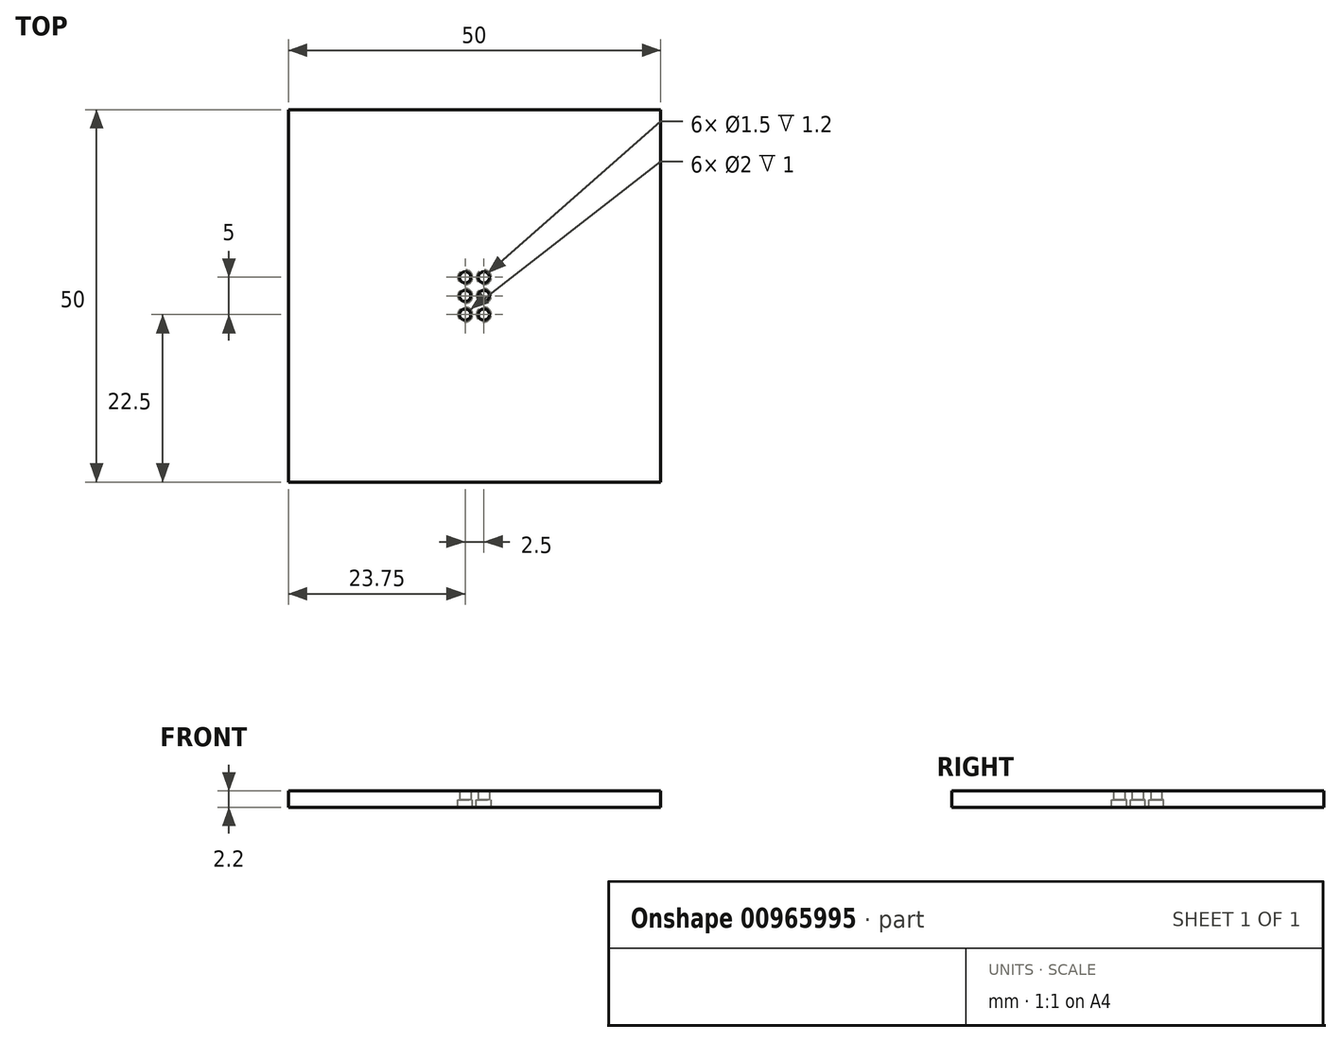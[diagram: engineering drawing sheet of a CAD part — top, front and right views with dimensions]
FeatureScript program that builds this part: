
annotation { "Feature Type Name" : "Feature", "Feature Type Description" : "" }
export const myFeature = defineFeature(function(context is Context, id is Id, definition is map)
    precondition{}
    {
        {
            var Q0;
            Q0=qCreatedBy(makeId("Top.planeOp"),FACE);
            var sketch = newSketch(context, id + "F0", { "sketchPlane" : qUnion([Q0])});
            skLineSegment(sketch, "E0.bottom", {"start": v(25, -25) * mm, "end": v(-25, -25) * mm});
            skLineSegment(sketch, "E0.top", {"start": v(25, 25) * mm, "end": v(-25, 25) * mm});
            skLineSegment(sketch, "E0.left", {"start": v(25, -25) * mm, "end": v(25, 25) * mm});
            skLineSegment(sketch, "E0.right", {"start": v(-25, -25) * mm, "end": v(-25, 25) * mm});
            skPoint(sketch, "E0.middle", {"position": v(0, 0) * mm});
            skCircle(sketch, "E1", {"center": v(-1.25, 0) * mm, "radius": 0.75 * mm});
            skCircle(sketch, "E2", {"center": v(-1.25, 2.5) * mm, "radius": 0.75 * mm});
            skCircle(sketch, "E3", {"center": v(-1.25, -2.5) * mm, "radius": 0.75 * mm});
            skCircle(sketch, "E4.MirrorC", {"center": v(1.25, 2.5) * mm, "radius": 0.75 * mm});
            skCircle(sketch, "E5.MirrorC", {"center": v(1.25, 0) * mm, "radius": 0.75 * mm});
            skCircle(sketch, "E6.MirrorC", {"center": v(1.25, -2.5) * mm, "radius": 0.75 * mm});
            skSolve(sketch);
        }
        {
            var Q0;
            Q0=makeQuery(id+"F0.imprint","IMPRINT",FACE,{"disambiguationData":[TD([[makeQuery(id+"F0.imprint","IMPRINT",EDGE,{"derivedFrom":sQuery(id+"F0.wireOp",EDGE,"E0.bottom")}),-1.0]])]});
            extrude(context, id + "F1", {"entities" : qUnion([Q0]), "depth" : 1.2 * mm, "offsetDistance" : 25 * mm});
        }
        {
            var Q0;
            Q0=makeQuery(id+"F1.opExtrude","CAP_FACE",FACE,{"disambiguationData":[OSD([sQuery(id+"F0.wireOp",EDGE,"E0.bottom"),sQuery(id+"F0.wireOp",EDGE,"E0.top"),sQuery(id+"F0.wireOp",EDGE,"E0.left"),sQuery(id+"F0.wireOp",EDGE,"E0.right"),sQuery(id+"F0.wireOp",EDGE,"E1"),sQuery(id+"F0.wireOp",EDGE,"E2"),sQuery(id+"F0.wireOp",EDGE,"E3"),sQuery(id+"F0.wireOp",EDGE,"E4.MirrorC"),sQuery(id+"F0.wireOp",EDGE,"E5.MirrorC"),sQuery(id+"F0.wireOp",EDGE,"E6.MirrorC")])],"isStart":true});
            var sketch = newSketch(context, id + "F2", { "sketchPlane" : qUnion([Q0])});
            skCircle(sketch, "E7", {"center": v(-1.25, 0) * mm, "radius": 1 * mm});
            skCircle(sketch, "E8", {"center": v(-1.25, 2.5) * mm, "radius": 1 * mm});
            skCircle(sketch, "E9", {"center": v(-1.25, -2.5) * mm, "radius": 1 * mm});
            skCircle(sketch, "E10.MirrorC", {"center": v(1.25, 2.5) * mm, "radius": 1 * mm});
            skCircle(sketch, "E11.MirrorC", {"center": v(1.25, 0) * mm, "radius": 1 * mm});
            skCircle(sketch, "E12.MirrorC", {"center": v(1.25, -2.5) * mm, "radius": 1 * mm});
            skSolve(sketch);
        }
        {
            var Q0;
            Q0=makeQuery(id+"F2.imprint","IMPRINT",FACE,{"disambiguationData":[TD([[makeQuery(id+"F2.imprint","IMPRINT",EDGE,{"derivedFrom":sQuery(id+"F2.wireOp",EDGE,"E7")}),-1.0]])]});
            extrude(context, id + "F3", {"entities" : qUnion([Q0]), "operationType" : NewBodyOperationType.ADD, "depth" : 1 * mm, "offsetDistance" : 25 * mm});
        }
    });
